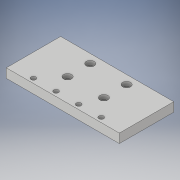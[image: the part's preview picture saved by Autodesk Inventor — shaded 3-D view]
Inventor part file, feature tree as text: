
AUTODESK INVENTOR PART (.ipt)
format: ipt  version: 2019 (Build 230136000, 136)  size: 142,848 bytes
history: native  units: mm
features: sketch x3, hole x2, extrude x1, projected_geometry x1
ambient origin geometry x8: Origin, YZ Plane, XZ Plane, XY Plane, X Axis, Y Axis, Z Axis, Center Point
bodies: Solid1 (feature_tree)
feature tree (7):
  extrude  "Extrusion1"  Depth=76.0mm
  hole  "Hole1"  [1 undecoded]
  hole  "Hole2"  [1 undecoded]
  sketch  "Sketch1"  dims[d0=158.0mm d1=76.0mm]
  sketch  "Sketch2"  dims[d2=12.7mm d3=0.0mm d4=50.8mm]
  projected_geometry  "Projected Loop1"
  sketch  "Sketch3"  dims[d5=50.8mm d6=31.75mm d8=6.756mm d9=6.0mm d10=11.113mm d11=6.35mm d12=90.0deg d13=8.0mm d14=20.594885mm d16=32.0mm d17=6.35mm d19=31.6mm d20=31.6mm d21=31.6mm d22=31.6mm d23=31.6mm d24=6.756mm d25=6.0mm d26=11.113mm d27=6.35mm d28=90.0deg d29=8.0mm d30=20.594885mm]
note: 2 required parameter values undecoded (feature->parameter linkage not recoverable at this tier; creation-order binding heuristic only, values carry confidence <= 0.55)
